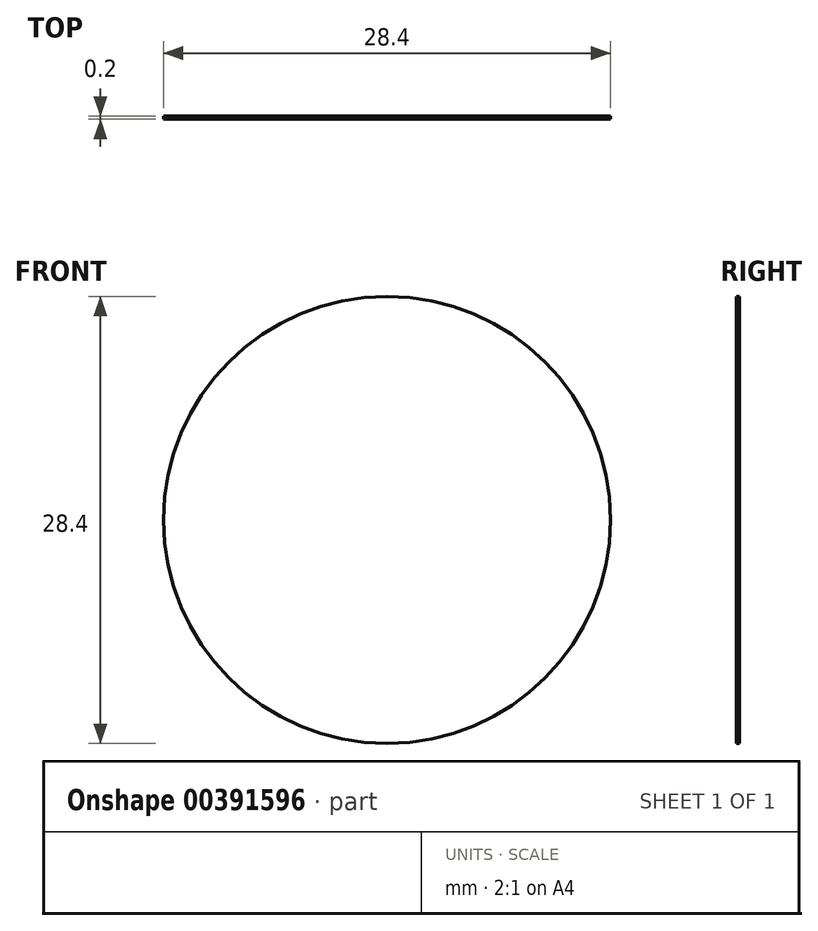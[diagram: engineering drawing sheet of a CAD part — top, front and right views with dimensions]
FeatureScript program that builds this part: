
annotation { "Feature Type Name" : "Feature", "Feature Type Description" : "" }
export const myFeature = defineFeature(function(context is Context, id is Id, definition is map)
    precondition{}
    {
        {
            var Q0;
            Q0=qCreatedBy(makeId("Front.planeOp"),FACE);
            var sketch = newSketch(context, id + "F0", { "sketchPlane" : qUnion([Q0])});
            skCircle(sketch, "E0", {"center": v(0, 0) * mm, "radius": 9 * mm, "construction": true});
            skCircle(sketch, "E1", {"center": v(0, 0) * mm, "radius": 10.5 * mm, "construction": true});
            skLineSegment(sketch, "E2", {"start": v(0, 9) * mm, "end": v(0.75, 9) * mm, "construction": true});
            skLineSegment(sketch, "E3", {"start": v(0.75, 9) * mm, "end": v(0.75, 13.5) * mm, "construction": true});
            skLineSegment(sketch, "E4", {"start": v(0.75, 13.5) * mm, "end": v(0, 13.5) * mm, "construction": true});
            skLineSegment(sketch, "E5", {"start": v(0, 13.5) * mm, "end": v(-0.75, 13.5) * mm, "construction": true});
            skLineSegment(sketch, "E6", {"start": v(-0.75, 13.5) * mm, "end": v(-0.75, 9) * mm, "construction": true});
            skLineSegment(sketch, "E7", {"start": v(-0.75, 9) * mm, "end": v(0, 9) * mm, "construction": true});
            skLineSegment(sketch, "E8.1.0", {"start": v(-3.85, 8.17) * mm, "end": v(-6.1, 12.07) * mm});
            skLineSegment(sketch, "E8.1.1", {"start": v(-7.4, 11.32) * mm, "end": v(-5.15, 7.42) * mm});
            skLineSegment(sketch, "E8.1.2", {"start": v(-5.15, 7.42) * mm, "end": v(-4.5, 7.8) * mm});
            skLineSegment(sketch, "E8.1.3", {"start": v(-4.5, 7.8) * mm, "end": v(-3.85, 8.17) * mm});
            skLineSegment(sketch, "E8.1.4", {"start": v(-6.1, 12.07) * mm, "end": v(-6.75, 11.7) * mm});
            skLineSegment(sketch, "E8.1.5", {"start": v(-6.75, 11.7) * mm, "end": v(-7.4, 11.32) * mm});
            skLineSegment(sketch, "E8.2.0", {"start": v(-7.42, 5.15) * mm, "end": v(-11.32, 7.4) * mm});
            skLineSegment(sketch, "E8.2.1", {"start": v(-12.07, 6.1) * mm, "end": v(-8.17, 3.85) * mm});
            skLineSegment(sketch, "E8.2.2", {"start": v(-8.17, 3.85) * mm, "end": v(-7.8, 4.5) * mm});
            skLineSegment(sketch, "E8.2.3", {"start": v(-7.8, 4.5) * mm, "end": v(-7.42, 5.15) * mm});
            skLineSegment(sketch, "E8.2.4", {"start": v(-11.32, 7.4) * mm, "end": v(-11.7, 6.75) * mm});
            skLineSegment(sketch, "E8.2.5", {"start": v(-11.7, 6.75) * mm, "end": v(-12.07, 6.1) * mm});
            skLineSegment(sketch, "E8.3.0", {"start": v(-9, 0.75) * mm, "end": v(-13.5, 0.75) * mm, "construction": true});
            skLineSegment(sketch, "E8.3.1", {"start": v(-13.5, -0.75) * mm, "end": v(-9, -0.75) * mm, "construction": true});
            skLineSegment(sketch, "E8.3.2", {"start": v(-9, -0.75) * mm, "end": v(-9, 0) * mm, "construction": true});
            skLineSegment(sketch, "E8.3.3", {"start": v(-9, 0) * mm, "end": v(-9, 0.75) * mm, "construction": true});
            skLineSegment(sketch, "E8.3.4", {"start": v(-13.5, 0.75) * mm, "end": v(-13.5, 0) * mm, "construction": true});
            skLineSegment(sketch, "E8.3.5", {"start": v(-13.5, 0) * mm, "end": v(-13.5, -0.75) * mm, "construction": true});
            skLineSegment(sketch, "E8.4.0", {"start": v(-8.17, -3.85) * mm, "end": v(-12.07, -6.1) * mm});
            skLineSegment(sketch, "E8.4.1", {"start": v(-11.32, -7.4) * mm, "end": v(-7.42, -5.15) * mm});
            skLineSegment(sketch, "E8.4.2", {"start": v(-7.42, -5.15) * mm, "end": v(-7.8, -4.5) * mm});
            skLineSegment(sketch, "E8.4.3", {"start": v(-7.8, -4.5) * mm, "end": v(-8.17, -3.85) * mm});
            skLineSegment(sketch, "E8.4.4", {"start": v(-12.07, -6.1) * mm, "end": v(-11.7, -6.75) * mm});
            skLineSegment(sketch, "E8.4.5", {"start": v(-11.7, -6.75) * mm, "end": v(-11.32, -7.4) * mm});
            skLineSegment(sketch, "E8.5.0", {"start": v(-5.15, -7.42) * mm, "end": v(-7.4, -11.32) * mm});
            skLineSegment(sketch, "E8.5.1", {"start": v(-6.1, -12.07) * mm, "end": v(-3.85, -8.17) * mm});
            skLineSegment(sketch, "E8.5.2", {"start": v(-3.85, -8.17) * mm, "end": v(-4.5, -7.8) * mm});
            skLineSegment(sketch, "E8.5.3", {"start": v(-4.5, -7.8) * mm, "end": v(-5.15, -7.42) * mm});
            skLineSegment(sketch, "E8.5.4", {"start": v(-7.4, -11.32) * mm, "end": v(-6.75, -11.7) * mm});
            skLineSegment(sketch, "E8.5.5", {"start": v(-6.75, -11.7) * mm, "end": v(-6.1, -12.07) * mm});
            skLineSegment(sketch, "E8.6.0", {"start": v(-0.75, -9) * mm, "end": v(-0.75, -13.5) * mm, "construction": true});
            skLineSegment(sketch, "E8.6.1", {"start": v(0.75, -13.5) * mm, "end": v(0.75, -9) * mm, "construction": true});
            skLineSegment(sketch, "E8.6.2", {"start": v(0.75, -9) * mm, "end": v(0, -9) * mm, "construction": true});
            skLineSegment(sketch, "E8.6.3", {"start": v(0, -9) * mm, "end": v(-0.75, -9) * mm, "construction": true});
            skLineSegment(sketch, "E8.6.4", {"start": v(-0.75, -13.5) * mm, "end": v(0, -13.5) * mm, "construction": true});
            skLineSegment(sketch, "E8.6.5", {"start": v(0, -13.5) * mm, "end": v(0.75, -13.5) * mm, "construction": true});
            skLineSegment(sketch, "E8.7.0", {"start": v(3.85, -8.17) * mm, "end": v(6.1, -12.07) * mm});
            skLineSegment(sketch, "E8.7.1", {"start": v(7.4, -11.32) * mm, "end": v(5.15, -7.42) * mm});
            skLineSegment(sketch, "E8.7.2", {"start": v(5.15, -7.42) * mm, "end": v(4.5, -7.8) * mm});
            skLineSegment(sketch, "E8.7.3", {"start": v(4.5, -7.8) * mm, "end": v(3.85, -8.17) * mm});
            skLineSegment(sketch, "E8.7.4", {"start": v(6.1, -12.07) * mm, "end": v(6.75, -11.7) * mm});
            skLineSegment(sketch, "E8.7.5", {"start": v(6.75, -11.7) * mm, "end": v(7.4, -11.32) * mm});
            skLineSegment(sketch, "E8.8.0", {"start": v(7.42, -5.15) * mm, "end": v(11.32, -7.4) * mm});
            skLineSegment(sketch, "E8.8.1", {"start": v(12.07, -6.1) * mm, "end": v(8.17, -3.85) * mm});
            skLineSegment(sketch, "E8.8.2", {"start": v(8.17, -3.85) * mm, "end": v(7.8, -4.5) * mm});
            skLineSegment(sketch, "E8.8.3", {"start": v(7.8, -4.5) * mm, "end": v(7.42, -5.15) * mm});
            skLineSegment(sketch, "E8.8.4", {"start": v(11.32, -7.4) * mm, "end": v(11.7, -6.75) * mm});
            skLineSegment(sketch, "E8.8.5", {"start": v(11.7, -6.75) * mm, "end": v(12.07, -6.1) * mm});
            skLineSegment(sketch, "E8.9.0", {"start": v(9, -0.75) * mm, "end": v(13.5, -0.75) * mm, "construction": true});
            skLineSegment(sketch, "E8.9.1", {"start": v(13.5, 0.75) * mm, "end": v(9, 0.75) * mm, "construction": true});
            skLineSegment(sketch, "E8.9.2", {"start": v(9, 0.75) * mm, "end": v(9, 0) * mm, "construction": true});
            skLineSegment(sketch, "E8.9.3", {"start": v(9, 0) * mm, "end": v(9, -0.75) * mm, "construction": true});
            skLineSegment(sketch, "E8.9.4", {"start": v(13.5, -0.75) * mm, "end": v(13.5, 0) * mm, "construction": true});
            skLineSegment(sketch, "E8.9.5", {"start": v(13.5, 0) * mm, "end": v(13.5, 0.75) * mm, "construction": true});
            skLineSegment(sketch, "E8.10.0", {"start": v(8.17, 3.85) * mm, "end": v(12.07, 6.1) * mm});
            skLineSegment(sketch, "E8.10.1", {"start": v(11.32, 7.4) * mm, "end": v(7.42, 5.15) * mm});
            skLineSegment(sketch, "E8.10.2", {"start": v(7.42, 5.15) * mm, "end": v(7.8, 4.5) * mm});
            skLineSegment(sketch, "E8.10.3", {"start": v(7.8, 4.5) * mm, "end": v(8.17, 3.85) * mm});
            skLineSegment(sketch, "E8.10.4", {"start": v(12.07, 6.1) * mm, "end": v(11.7, 6.75) * mm});
            skLineSegment(sketch, "E8.10.5", {"start": v(11.7, 6.75) * mm, "end": v(11.32, 7.4) * mm});
            skLineSegment(sketch, "E8.11.0", {"start": v(5.15, 7.42) * mm, "end": v(7.4, 11.32) * mm});
            skLineSegment(sketch, "E8.11.1", {"start": v(6.1, 12.07) * mm, "end": v(3.85, 8.17) * mm});
            skLineSegment(sketch, "E8.11.2", {"start": v(3.85, 8.17) * mm, "end": v(4.5, 7.8) * mm});
            skLineSegment(sketch, "E8.11.3", {"start": v(4.5, 7.8) * mm, "end": v(5.15, 7.42) * mm});
            skLineSegment(sketch, "E8.11.4", {"start": v(7.4, 11.32) * mm, "end": v(6.75, 11.7) * mm});
            skLineSegment(sketch, "E8.11.5", {"start": v(6.75, 11.7) * mm, "end": v(6.1, 12.07) * mm});
            skCircle(sketch, "E9", {"center": v(0, 0) * mm, "radius": 13.5 * mm, "construction": true});
            skSolve(sketch);
        }
        {
            var Q0;
            Q0=qCreatedBy(makeId("Front.planeOp"),FACE);
            var sketch = newSketch(context, id + "F1", { "sketchPlane" : qUnion([Q0])});
            skText(sketch, "E10", { "text": "12", "fontName": "AllertaStencil-Regular.ttf"});
            skText(sketch, "E11", { "text": "6", "fontName": "AllertaStencil-Regular.ttf"});
            skText(sketch, "E12", { "text": "9", "fontName": "AllertaStencil-Regular.ttf"});
            skPoint(sketch, "E13", {"position": v(-10.5, -0.12) * mm});
            skText(sketch, "E14", { "text": "3", "fontName": "AllertaStencil-Regular.ttf"});
            skCircle(sketch, "E15", {"center": v(0, 0) * mm, "radius": 10.5 * mm, "construction": true});
            skCircle(sketch, "E16", {"center": v(0, 0) * mm, "radius": 7 * mm, "construction": true});
            skLineSegment(sketch, "E17", {"start": v(0, 0) * mm, "end": v(-0.12, 10.5) * mm, "construction": true});
            skLineSegment(sketch, "E18.1.0", {"start": v(0, 0) * mm, "end": v(-10.5, -0.12) * mm, "construction": true});
            skLineSegment(sketch, "E18.2.0", {"start": v(0, 0) * mm, "end": v(0.12, -10.5) * mm, "construction": true});
            skLineSegment(sketch, "E18.3.0", {"start": v(0, 0) * mm, "end": v(10.5, 0.12) * mm, "construction": true});
            skPoint(sketch, "E19", {"position": v(10.5, 0.12) * mm});
            const initialGuessF1  = {"E10": [-0.00258, 0.007, 1, 0, 0.0035], "E11": [-0.0014, -0.0105, 1, 0, 0.0035], "E12": [-0.0105, -0.00187, 1, 0, 0.0035], "E14": [0.00776, -0.00163, 1, 0, 0.0035]};
            skSetInitialGuess(sketch, initialGuessF1);
            skSolve(sketch);
        }
        {
            var Q0;
            Q0=qCreatedBy(makeId("Front.planeOp"),FACE);
            var sketch = newSketch(context, id + "F2", { "sketchPlane" : qUnion([Q0])});
            skLineSegment(sketch, "E20", {"start": v(0, 10.42) * mm, "end": v(1.75, 13.46) * mm});
            skLineSegment(sketch, "E21", {"start": v(1.75, 13.46) * mm, "end": v(-1.75, 13.46) * mm});
            skLineSegment(sketch, "E22", {"start": v(-1.75, 13.46) * mm, "end": v(0, 10.42) * mm});
            skLineSegment(sketch, "E23", {"start": v(-10.96, 0) * mm, "end": v(-10.96, 1) * mm});
            skLineSegment(sketch, "E24", {"start": v(-10.96, 1) * mm, "end": v(-13.46, 1) * mm});
            skLineSegment(sketch, "E25", {"start": v(-13.46, 1) * mm, "end": v(-13.46, -1) * mm});
            skLineSegment(sketch, "E26", {"start": v(-13.46, -1) * mm, "end": v(-10.96, -1) * mm});
            skLineSegment(sketch, "E27", {"start": v(-10.96, -1) * mm, "end": v(-10.96, 0) * mm});
            skCircle(sketch, "E28", {"center": v(0, 0) * mm, "radius": 11.25 * mm, "construction": true});
            skLineSegment(sketch, "E29.1.0", {"start": v(-1, -10.96) * mm, "end": v(-1, -13.46) * mm});
            skLineSegment(sketch, "E29.1.1", {"start": v(-1, -13.46) * mm, "end": v(1, -13.46) * mm});
            skLineSegment(sketch, "E29.1.2", {"start": v(1, -13.46) * mm, "end": v(1, -10.96) * mm});
            skLineSegment(sketch, "E29.1.3", {"start": v(1, -10.96) * mm, "end": v(0, -10.96) * mm});
            skLineSegment(sketch, "E29.1.4", {"start": v(0, -10.96) * mm, "end": v(-1, -10.96) * mm});
            skLineSegment(sketch, "E29.2.0", {"start": v(10.96, -1) * mm, "end": v(13.46, -1) * mm});
            skLineSegment(sketch, "E29.2.1", {"start": v(13.46, -1) * mm, "end": v(13.46, 1) * mm});
            skLineSegment(sketch, "E29.2.2", {"start": v(13.46, 1) * mm, "end": v(10.96, 1) * mm});
            skLineSegment(sketch, "E29.2.3", {"start": v(10.96, 1) * mm, "end": v(10.96, 0) * mm});
            skLineSegment(sketch, "E29.2.4", {"start": v(10.96, 0) * mm, "end": v(10.96, -1) * mm});
            skLineSegment(sketch, "E29.anchor1", {"start": v(0, 0) * mm, "end": v(-10.96, 0) * mm, "construction": true});
            skLineSegment(sketch, "E29.anchor2", {"start": v(0, 0) * mm, "end": v(10.96, 0) * mm, "construction": true});
            skCircle(sketch, "E30", {"center": v(0, 0) * mm, "radius": 14.2 * mm, "construction": true});
            skCircle(sketch, "E31", {"center": v(0, 0) * mm, "radius": 13.5 * mm, "construction": true});
            skLineSegment(sketch, "E32", {"start": v(0, 13.5) * mm, "end": v(0, 11.25) * mm, "construction": true});
            skCircle(sketch, "E33", {"center": v(0, 12.38) * mm, "radius": 1.13 * mm, "construction": true});
            skCircle(sketch, "E34.1.0", {"center": v(-6.19, 10.72) * mm, "radius": 1.13 * mm, "construction": true});
            skCircle(sketch, "E34.2.0", {"center": v(-10.72, 6.19) * mm, "radius": 1.13 * mm, "construction": true});
            skCircle(sketch, "E34.3.0", {"center": v(-12.38, 0) * mm, "radius": 1.13 * mm, "construction": true});
            skCircle(sketch, "E34.4.0", {"center": v(-10.72, -6.19) * mm, "radius": 1.13 * mm, "construction": true});
            skCircle(sketch, "E34.5.0", {"center": v(-6.19, -10.72) * mm, "radius": 1.13 * mm, "construction": true});
            skCircle(sketch, "E34.6.0", {"center": v(0, -12.38) * mm, "radius": 1.13 * mm, "construction": true});
            skCircle(sketch, "E34.7.0", {"center": v(6.19, -10.72) * mm, "radius": 1.13 * mm, "construction": true});
            skCircle(sketch, "E34.8.0", {"center": v(10.72, -6.19) * mm, "radius": 1.13 * mm, "construction": true});
            skCircle(sketch, "E34.9.0", {"center": v(12.38, 0) * mm, "radius": 1.13 * mm, "construction": true});
            skCircle(sketch, "E34.10.0", {"center": v(10.72, 6.19) * mm, "radius": 1.13 * mm, "construction": true});
            skCircle(sketch, "E34.11.0", {"center": v(6.19, 10.72) * mm, "radius": 1.13 * mm, "construction": true});
            skSolve(sketch);
        }
        {
            var Q0;
            Q0=qCreatedBy(makeId("Front.planeOp"),FACE);
            var sketch = newSketch(context, id + "F3", { "sketchPlane" : qUnion([Q0])});
            skCircle(sketch, "E35", {"center": v(0, 0) * mm, "radius": 14.2 * mm});
            skSolve(sketch);
        }
        {
            var Q0;
            Q0=qCreatedBy(makeId("Front.planeOp"),FACE);
            var sketch = newSketch(context, id + "F4", { "sketchPlane" : qUnion([Q0])});
            skCircle(sketch, "E36", {"center": v(0, 0) * mm, "radius": 8 * mm, "construction": true});
            skCircle(sketch, "E37", {"center": v(0, 8) * mm, "radius": 0.75 * mm, "construction": true});
            skCircle(sketch, "E38.1.0", {"center": v(-4, 6.93) * mm, "radius": 0.75 * mm});
            skCircle(sketch, "E38.2.0", {"center": v(-6.93, 4) * mm, "radius": 0.75 * mm});
            skCircle(sketch, "E38.3.0", {"center": v(-8, 0) * mm, "radius": 0.75 * mm, "construction": true});
            skCircle(sketch, "E38.4.0", {"center": v(-6.93, -4) * mm, "radius": 0.75 * mm});
            skCircle(sketch, "E38.5.0", {"center": v(-4, -6.93) * mm, "radius": 0.75 * mm});
            skCircle(sketch, "E38.6.0", {"center": v(0, -8) * mm, "radius": 0.75 * mm, "construction": true});
            skCircle(sketch, "E38.7.0", {"center": v(4, -6.93) * mm, "radius": 0.75 * mm});
            skCircle(sketch, "E38.8.0", {"center": v(6.93, -4) * mm, "radius": 0.75 * mm});
            skCircle(sketch, "E38.9.0", {"center": v(8, 0) * mm, "radius": 0.75 * mm, "construction": true});
            skCircle(sketch, "E38.10.0", {"center": v(6.93, 4) * mm, "radius": 0.75 * mm});
            skCircle(sketch, "E38.11.0", {"center": v(4, 6.93) * mm, "radius": 0.75 * mm});
            skSolve(sketch);
        }
        {
            var Q0;
            Q0=qSketchRegion(id+"F3",true);
            extrude(context, id + "F5", {"entities" : qUnion([Q0]), "depth" : 0.2 * mm});
        }
    });
